# Revit family: Millie UL
name_source: partatom
category: Lighting Fixtures
units: mm (PartAtom-declared; Revit-internal decimal feet)

## family parameters
Always vertical = Yes
Cut with Voids When Loaded = No
Host = Wall
Light Source = No
Maintain Annotation Orientation = No
OmniClass Number = 23.80.70.00
OmniClass Title = Lighting
Part Type = Normal
Room Calculation Point = No
Round Connector Dimension = Use Diameter
Shared = No

## types (2) — shared parameters
Dimmable = Yes
Dimming Method = Lamp dependant
Driver Included = No
Driver Required = No
Efficacy (lm/w) = Lamp dependant
Lamp = LED
Light Source Fixed = Yes
Main Finish = Various
Main Material = Metal - Zinc
Manufacturer = Astro Lighting Ltd
Manufacturer URL - Europe and Rest of World = www.astrolighting.com
Manufacturer URL - North America = us.astrolighting.com
Power (Watts) = Lamp dependant
Product CCT = 2700K / 3000K
Product CRI = 80 / 90
Product Weight (KG) = 1.294
URL = www.astrolighting.com
zero-valued in all types: Default Elevation

## per-type parameters (varying)
| type | ADA compliant | Electrical Class | Location / IP Rating | Product Location | Product SKU |
| CE | N / A | 2 | IP44 | Bathroom/indoor | 1454001 |
| ETL |  | 1 | DAMP | Bathroom/Indoor | 1454004 |

## geometry (parser evidence)
native form markers: Sweep x3
no freeform markers — native parametric forms only
